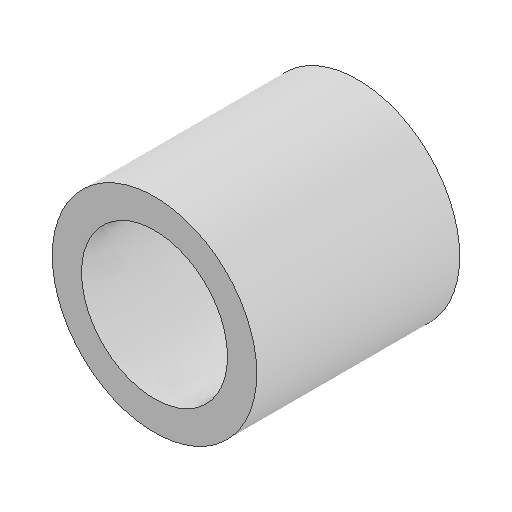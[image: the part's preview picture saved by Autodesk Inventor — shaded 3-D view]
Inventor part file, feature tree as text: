
AUTODESK INVENTOR PART (.ipt)
format: ipt  version: 2025.1 (Build 291241000, 241)  size: 100,864 bytes
history: native  units: mm
features: other x1, extrude x1, sketch x1
ambient origin geometry x8: Origin, YZ Plane, XZ Plane, XY Plane, X Axis, Y Axis, Z Axis, Center Point
bodies: Body1 (feature_tree)
feature tree (3):
  other  "Bryła1"
  extrude  "Wyciągnięcie proste1"  Depth=5.0mm
  sketch  "Szkic1"
